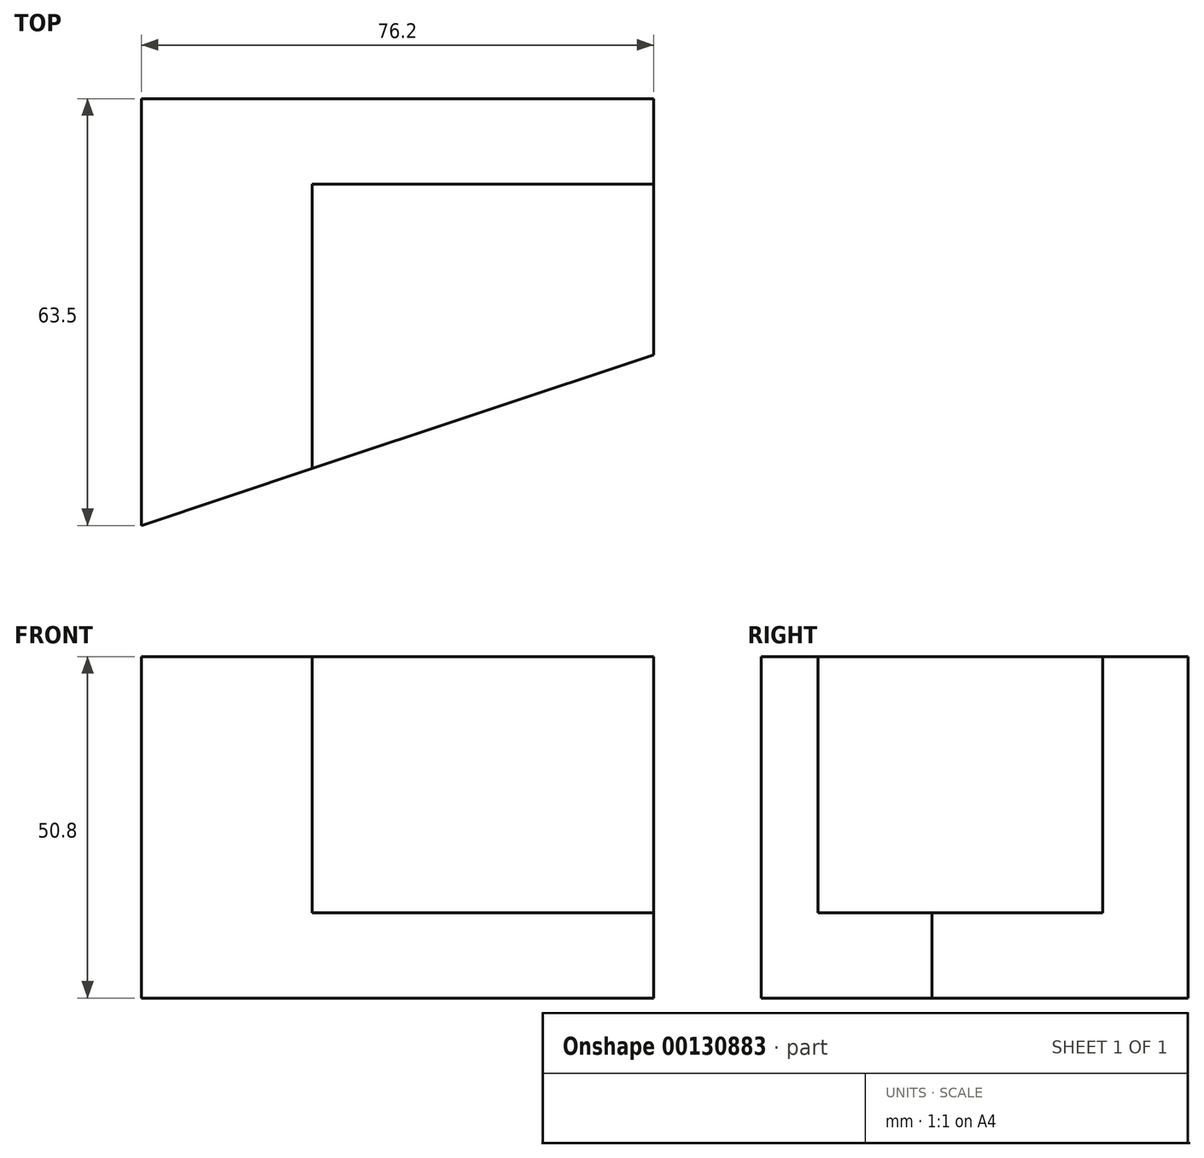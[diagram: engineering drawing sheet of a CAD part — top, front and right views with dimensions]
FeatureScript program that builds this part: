
annotation { "Feature Type Name" : "Feature", "Feature Type Description" : "" }
export const myFeature = defineFeature(function(context is Context, id is Id, definition is map)
    precondition{}
    {
        {
            var Q0;
            Q0=qCreatedBy(makeId("Front.planeOp"),FACE);
            var sketch = newSketch(context, id + "F0", { "sketchPlane" : qUnion([Q0])});
            skLineSegment(sketch, "E0.bottom", {"start": v(0, 0) * mm, "end": v(76.2, 0) * mm});
            skLineSegment(sketch, "E0.top", {"start": v(0, 50.8) * mm, "end": v(76.2, 50.8) * mm});
            skLineSegment(sketch, "E0.left", {"start": v(0, 0) * mm, "end": v(0, 50.8) * mm});
            skLineSegment(sketch, "E0.right", {"start": v(76.2, 0) * mm, "end": v(76.2, 50.8) * mm});
            skLineSegment(sketch, "E1", {"start": v(25.4, 50.8) * mm, "end": v(25.4, 12.7) * mm});
            skLineSegment(sketch, "E2", {"start": v(25.4, 12.7) * mm, "end": v(76.2, 12.7) * mm});
            skSolve(sketch);
        }
        {
            var Q0;
            {var subQ1=sQuery(id+"F0.wireOp",EDGE,"E0.bottom");Q0=makeQuery(id+"F0.imprint","IMPRINT",FACE,{"disambiguationData":[TD([[makeQuery(id+"F0.imprint","IMPRINT",EDGE,{"derivedFrom":subQ1}),1.0]])]});}
            extrude(context, id + "F1", {"entities" : qUnion([Q0]), "depth" : 63.5 * mm});
        }
        {
            var Q0;
            Q0 = qSketchRegion(id + "F0", true);
            extrude(context, id + "F2", {"entities" : qUnion([Q0]), "operationType" : NewBodyOperationType.ADD, "depth" : 12.7 * mm});
        }
        {
            var Q0;
            {var subQ0=sQuery(id+"F0.wireOp",EDGE,"E0.top");Q0=makeQuery(id+"F2.boolean.opBoolean","MERGE",FACE,{"derivedFrom":[makeQuery(id+"F1.opExtrude","SWEPT_FACE",FACE,{"disambiguationData":[OSD([subQ0])]}),makeQuery(id+"F2.opExtrude","SWEPT_FACE",FACE,{"disambiguationData":[OSD([subQ0])]})]});}
            var sketch = newSketch(context, id + "F3", { "sketchPlane" : qUnion([Q0])});
            skLineSegment(sketch, "E3", {"start": v(0, -63.5) * mm, "end": v(76.2, -63.5) * mm});
            skLineSegment(sketch, "E4", {"start": v(76.2, -63.5) * mm, "end": v(76.2, -38.1) * mm});
            skLineSegment(sketch, "E5", {"start": v(76.2, -38.1) * mm, "end": v(0, -63.5) * mm});
            skSolve(sketch);
        }
        {
            var Q0;
            {var subQ1=sQuery(id+"F3.wireOp",EDGE,"E3");var subQ2=sQuery(id+"F0.wireOp",EDGE,"E0.top");var subQ4=makeQuery(id+"F1.opExtrude","SWEPT_EDGE",EDGE,{"disambiguationData":[OSD([subQ2,sQuery(id+"F0.wireOp",EDGE,"E1")])]});var subQ5=makeQuery(id+"F3.imprint","INTERSECT",VERTEX,{"derivedFrom":[subQ4,subQ1]});Q0=makeQuery(id+"F3.imprint","IMPRINT",FACE,{"disambiguationData":[TD([[makeQuery(id+"F3.imprint","IMPRINT",EDGE,{"disambiguationData":[TD([[subQ5,1.0]])],"derivedFrom":subQ1}),1.0]])]});}
            var Q1;
            {var subQ3=sQuery(id+"F3.wireOp",EDGE,"E4");Q1=makeQuery(id+"F3.imprint","IMPRINT",FACE,{"disambiguationData":[TD([[makeQuery(id+"F3.imprint","IMPRINT",EDGE,{"derivedFrom":subQ3}),1.0]])]});}
            extrude(context, id + "F4", {"entities" : qUnion([Q0, Q1]), "operationType" : NewBodyOperationType.REMOVE, "endBound" : BoundingType.THROUGH_ALL, "oppositeDirection" : true, "depth" : 25.4 * mm});
        }
    });
